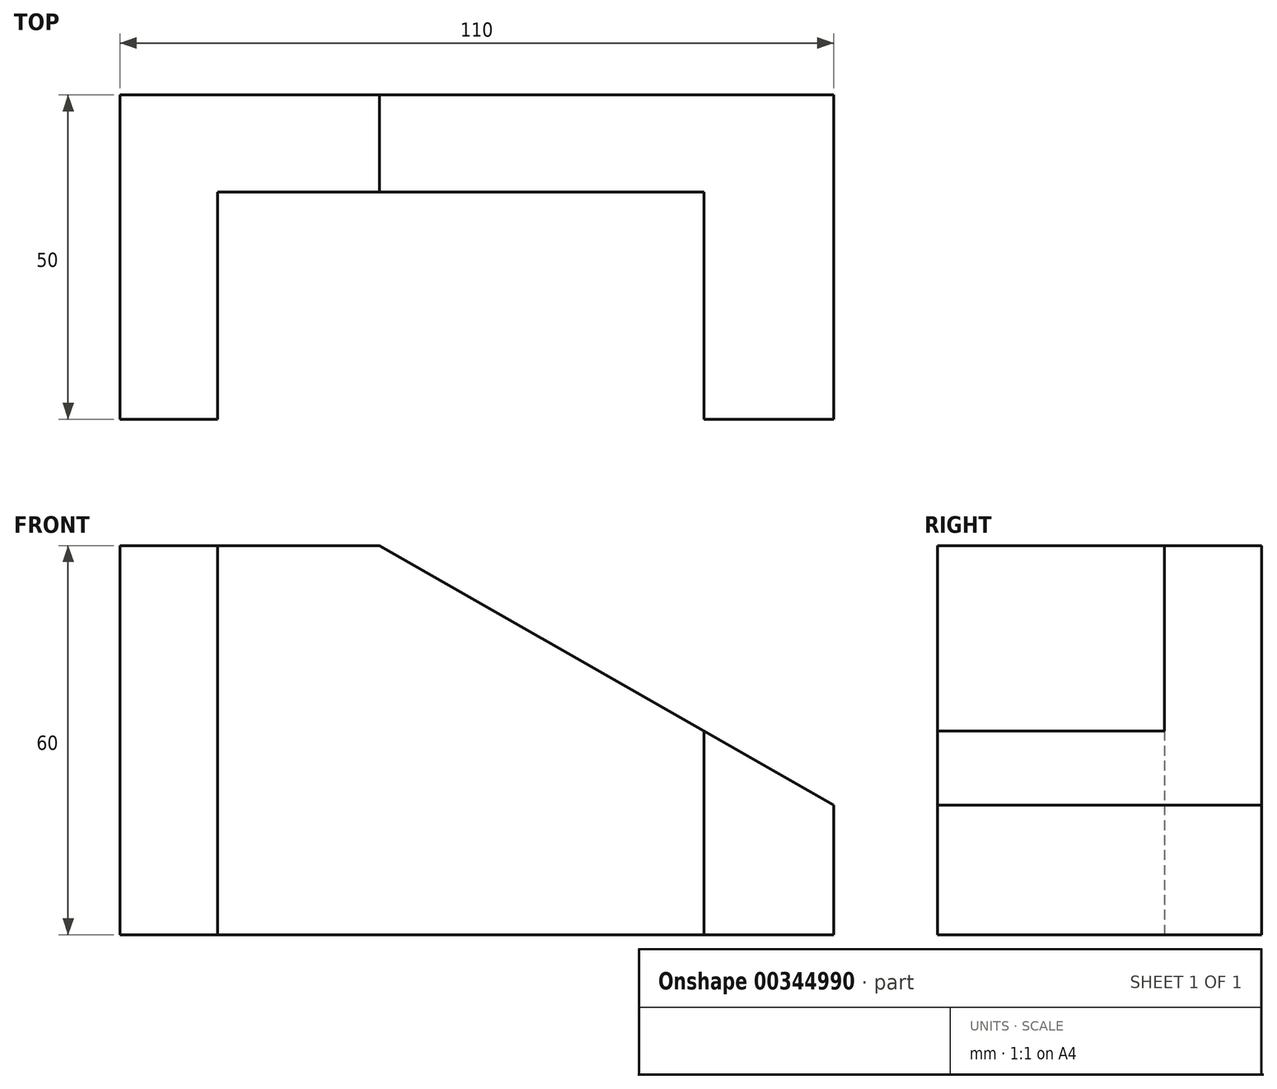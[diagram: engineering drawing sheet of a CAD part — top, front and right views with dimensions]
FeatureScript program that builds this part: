
annotation { "Feature Type Name" : "Feature", "Feature Type Description" : "" }
export const myFeature = defineFeature(function(context is Context, id is Id, definition is map)
    precondition{}
    {
        {
            var Q0;
            Q0=qCreatedBy(makeId("Top.planeOp"),FACE);
            var sketch = newSketch(context, id + "F0", { "sketchPlane" : qUnion([Q0])});
            skLineSegment(sketch, "E0.bottom", {"start": v(55, 25) * mm, "end": v(-55, 25) * mm});
            skLineSegment(sketch, "E0.top", {"start": v(55, -25) * mm, "end": v(35, -25) * mm});
            skLineSegment(sketch, "E0.left", {"start": v(55, 25) * mm, "end": v(55, -25) * mm});
            skLineSegment(sketch, "E0.right", {"start": v(-55, 25) * mm, "end": v(-55, -25) * mm});
            skPoint(sketch, "E0.middle", {"position": v(0, 0) * mm});
            skLineSegment(sketch, "E1", {"start": v(35, 25) * mm, "end": v(35, -25) * mm});
            skLineSegment(sketch, "E2", {"start": v(-40, 25) * mm, "end": v(-40, -25) * mm});
            skLineSegment(sketch, "E3", {"start": v(-55, 10) * mm, "end": v(55, 10) * mm});
            skLineSegment(sketch, "E4.trimOffspring", {"start": v(-40, -25) * mm, "end": v(-55, -25) * mm});
            skSolve(sketch);
        }
        {
            var Q0;
            Q0 = qSketchRegion(id + "F0", true);
            extrude(context, id + "F1", {"entities" : qUnion([Q0]), "depth" : 60 * mm});
        }
        {
            var Q0;
            Q0=makeQuery(id+"F1.opExtrude","SWEPT_FACE",FACE,{"disambiguationData":[OSD([sQuery(id+"F0.wireOp",EDGE,"E0.top")])]});
            var sketch = newSketch(context, id + "F2", { "sketchPlane" : qUnion([Q0])});
            skPoint(sketch, "E5", {"position": v(55, 20) * mm});
            skPoint(sketch, "E6", {"position": v(-15, 60) * mm});
            skLineSegment(sketch, "E7", {"start": v(-15, 60) * mm, "end": v(55, 20) * mm});
            skLineSegment(sketch, "E8", {"start": v(55, 60) * mm, "end": v(-15, 60) * mm});
            skLineSegment(sketch, "E9.0", {"start": v(55, 60) * mm, "end": v(55, 20) * mm});
            skPoint(sketch, "E10.orphan", {"position": v(55, 0) * mm});
            skSolve(sketch);
        }
        {
            var Q0;
            Q0 = qSketchRegion(id + "F2", true);
            extrude(context, id + "F3", {"entities" : qUnion([Q0]), "operationType" : NewBodyOperationType.REMOVE, "oppositeDirection" : true, "depth" : 50 * mm});
        }
    });
